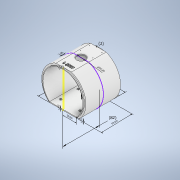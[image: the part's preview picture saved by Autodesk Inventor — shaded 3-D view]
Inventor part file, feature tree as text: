
AUTODESK INVENTOR PART (.ipt)
format: ipt  version: 2020 (Build 240168000, 168)  size: 487,936 bytes
history: native  units: mm
features: sketch x18, other x12, extrude x9, hole x5, plane x1
ambient origin geometry x8: Origin, YZ Plane, XZ Plane, XY Plane, X Axis, Y Axis, Z Axis, Center Point
bodies: Solid1 (feature_tree)
feature tree (45):
  other  "Annotations"
  sketch  "Sketch1"  dims[d8=82.0mm d9=18.0mm d10=0.0mm d11=0.0mm d12=78.0mm d13=0.0mm]
  sketch  "Sketch2"  dims[d19=59.393877mm d64=2.0mm]
  extrude  "Extrusion1"  Depth=78.0mm TaperAngle=0.0deg
  extrude  "Extrusion2"  Depth=2.0mm
  sketch  "Sketch25"  dims[d65=2.0mm d66=82.0mm]
  sketch  "Sketch26"  dims[d67=35.0mm d69=20.0mm]
  plane  "Work Plane8"
  extrude  "Extrusion8"  Depth=82.0mm
  extrude  "Extrusion9"  Depth=20.0mm
  sketch  "Sketch43"  dims[d174=50.0mm d178=70.0mm]
  sketch  "Sketch44"  dims[d182=1.403953mm d185=1.0mm]
  extrude  "Extrusion13"  Depth=0.25mm TaperAngle=0.0deg
  extrude  "Extrusion14"  Depth=50.0mm
  extrude  "Extrusion15"  Depth=70.0mm
  hole  "Hole8"  [1 undecoded]
  hole  "Hole9"  [1 undecoded]
  extrude  "Extrusion16"  Depth=6.0mm
  extrude  "Extrusion18"  Depth=3.0mm
  hole  "Hole10"  [1 undecoded]
  hole  "Hole11"  [1 undecoded]
  hole  "Hole12"  [1 undecoded]
  sketch  "Sketch27"  dims[d70=9.25mm d71=0.0mm d77=0.25mm d78=0.0mm]
  sketch  "Sketch29"  dims[d171=60.0mm d173=50.0mm]
  sketch  "Sketch45"  dims[d186=69.0mm d187=0.0mm d188=11.0mm d189=0.0mm]
  sketch  "Sketch46"  dims[d192=35.96mm d194=6.0mm]
  sketch  "Sketch47"  dims[d195=7.3mm d196=3.0mm]
  sketch  "Sketch50"  dims[d197=3.0mm d198=3.0mm d199=0.0mm]
  sketch  "Sketch51"  dims[d200=3.0mm d201=6.0mm d202=4.0mm d203=2.0mm d204=90.0deg d205=10.5mm d206=20.594885mm]
  sketch  "Sketch53"  dims[d207=3.0mm d208=6.0mm d209=4.0mm d210=2.0mm d211=90.0deg d212=10.5mm d213=20.594885mm d219=5.0mm d220=0.0mm]
  sketch  "Sketch54"  dims[d223=6.0mm d224=0.0mm]
  sketch  "Sketch55"  dims[d232=15.0mm d233=6.0mm d234=4.0mm d235=2.0mm d236=90.0deg d237=10.5mm d238=20.594885mm d262=14.525mm]
  sketch  "Sketch56"  dims[d263=15.0mm]
  sketch  "Sketch57"  dims[d264=14.525mm d265=15.0mm d266=2.3mm d267=14.95mm d268=7.5mm d269=2.3mm d270=37.5mm d271=2.3mm d272=7.5mm d273=2.3mm d277=2.3mm d278=6.0mm d279=5.0mm d280=0.7mm d281=90.0deg d282=15.664mm d283=0.0mm d291=20.0mm d292=2.0mm d293=2.0mm d294=23.5mm d295=1.0mm d296=1.5mm d297=1.5mm d298=1.0mm d299=1.5mm d300=1.0mm d301=1.5mm d302=1.5mm d303=1.0mm d304=1.0mm d305=6.0mm d306=5.0mm d307=0.7mm d308=90.0deg d309=10.5mm d310=20.594885mm d214=4.992417mm d215=30.083211mm d216=7.594445mm d217=2.441621mm d218=1.934335mm d228=9.517749mm d229=0.948594mm d230=69.027108mm d239=6.080937mm d240=3.441722mm d241=70.0mm d245=2.911617mm d246=9.26364mm d247=20.000012mm d248=3.423786mm d249=8.043699mm d250=91.000003mm d251=2.418403mm d252=7.765244mm d253=14.000018mm d259=1.931685mm d260=6.842692mm d261=3.0mm d274=4.154549mm d275=5.82758mm d276=1.934335mm d285=2.0mm d288=29.760345mm d289=20.0mm d30=0.5mm d31=0.872665mm d32=0.5mm d33=0.872665mm d79=0.5mm d80=0.872665mm d93=1.0mm d94=1.0mm d95=1.0mm d96=0.15mm d97=5.0mm d98=0.375mm d99=14.3117mm d100=0.75mm d101=20.594885mm d102=0.0625mm d103=0.75mm d104=0.375mm d159=0.5mm d160=0.872665mm d161=0.5mm d162=0.872665mm d172=0.872665mm d179=0.5mm d180=0.872665mm d181=0.5mm d184=0.5mm d221=0.5mm d222=0.872665mm d254=0.5mm d255=0.872665mm d256=0.5mm d257=0.872665mm]
  other  "Linear Dimension 2"
  other  "Linear Dimension 3"
  other  "Linear Dimension 5"
  other  "Linear Dimension 6"
  other  "Linear Dimension 7"
  other  "Linear Dimension 8"
  other  "Linear Dimension 9"
  other  "Linear Dimension 12"
  other  "Linear Dimension 13"
  other  "Linear Dimension 14"
  other  "Diameter Dimension 2"
note: 5 required parameter values undecoded (feature->parameter linkage not recoverable at this tier; creation-order binding heuristic only, values carry confidence <= 0.55)
